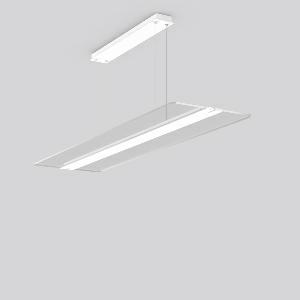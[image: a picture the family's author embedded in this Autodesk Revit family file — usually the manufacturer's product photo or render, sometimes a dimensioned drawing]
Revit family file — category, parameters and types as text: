
# Revit family: twindot_s_312263_002_76_26a1
name_source: partatom
category: Lighting Fixtures
units: mm (PartAtom-declared; Revit-internal decimal feet)

## family parameters
Cut with Voids When Loaded = No
Host = Face
Light Source = No
Part Type = Normal
Room Calculation Point = No
Round Connector Dimension = Use Diameter
Shared = No

## types (1)
- TWINDOT S (1 x LED Modul 830, 6500 lm, 3000)
    Apparent Load = 57 VA
    CIE Flux Codes = 47 77 94 55 100
    Color Rendering = 80
    Color Temperature = 3000
    Default Elevation = 1800 mm
    Description = Series: TWINDOT S
LED pendant luminaire with extremely flat and frameless appearance. Middle bar made of aluminium extrusion profile, powder-coated. Transparent light guide made of UV-resistant acrylic glass (PMMA) with TWINDOT prismatic. Light control with perfectly glare-free TWINDOT technology for pleasantly gentle light with soft shadows. Even and wide indirect and direct light distribution. Direct 55%, indirect 45% light emission. 4-point steel cable suspension, steplessly adjustable. Converter integrated in the canopy (powder-coated white). Power supply through suspension cable. 
Colour: traffic white, matt (RAL 9016)
Length: 1200 mm
Width: 350 mm
Height: 20 mm
Suspension length: 500-1200 mm
Lamp: LED
Socket: without socket
Colour temperature: 3000K
Colour rendering index (CRI): 80
System power: 57 W
Rated luminous flux: 6500 lm
Luminous efficiency: 114 lm/W
Control gear: Converter, dimmable, DALI
Protection class: I
Type of protection: IP 20
    Height = 20 mm  [stored 0.0656168 ft]
    Lamp = 1 x LED Modul 830
    Lamp Light Flux = 6500 lm
    Lamp count = 1
    Length = 1200 mm
    Lifetime = 50000 h
    Luminous efficacy = 114 lm/W
    Manufacturer = RZB
    ModVariant = No
    Model = 312263.002.76
    Mounting Place = Ceiling
    Mounting Type = Pendant
    Number of Poles = 1
    OnlyDefault = Yes
    Power Factor = 1
    Product Name = TWINDOT S
    Product group = Pendant modular luminaires
    ProductGroupID = 906
    Protection Class = Protection class I
    Protection Degree = IP 20
    RLX_Detail_Level = 1
    RLX_Emergency_Light_Flux = 0 lm
    RLX_Emergency_Type = 0
    RLX_Emergency_Type_DB = No
    RlxData = <blob elided: 35325 chars, md5=622f87d9>
    Socket = socket
    Standby Power = 0 W
    System Light Flux = 6500 lm
    System Power = 57 W
    Type Comments = Product without accessories
    Type Image = 312263.002.jpg
    URL = http://relux.com
    VarID = ---
    Voltage = 230 V
    Voltage Range = 220-240 V
    Weight = 0.00 kg
    Width = 350 mm

note: [stored X ft] marks values corroborated as IEEE doubles in the binary element streams (Revit-internal decimal feet)

## geometry (parser evidence)
native form markers: Blend x4, Sweep x9
no freeform markers — native parametric forms only
